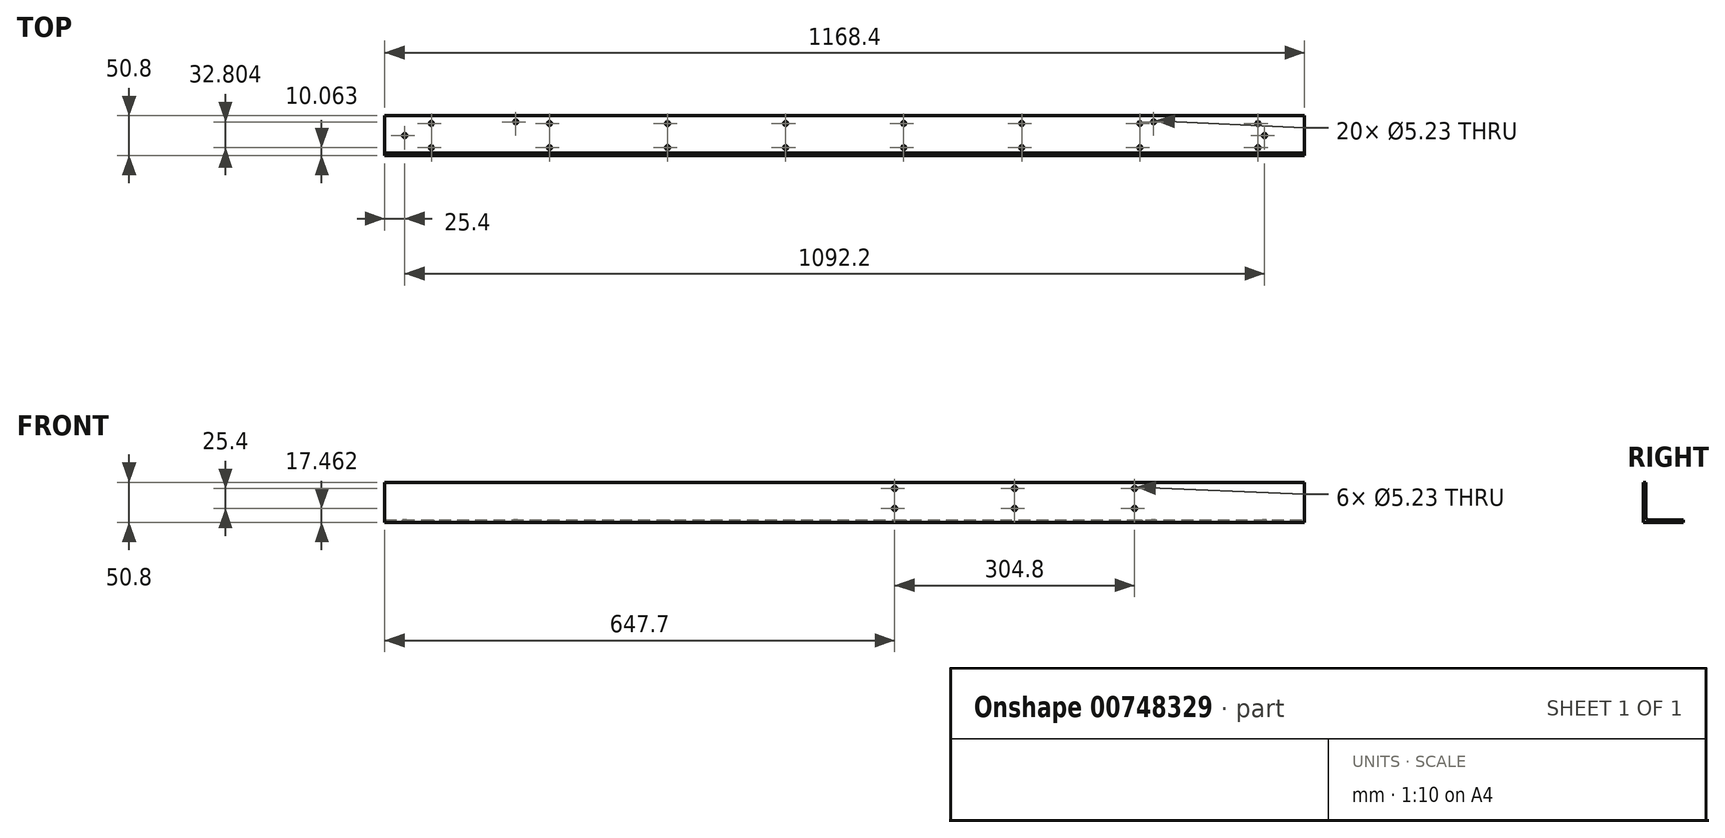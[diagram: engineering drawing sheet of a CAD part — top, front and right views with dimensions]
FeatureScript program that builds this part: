
annotation { "Feature Type Name" : "Feature", "Feature Type Description" : "" }
export const myFeature = defineFeature(function(context is Context, id is Id, definition is map)
    precondition{}
    {
        {
            var Q0;
            Q0=qCreatedBy(makeId("Right.planeOp"),FACE);
            var sketch = newSketch(context, id + "F0", { "sketchPlane" : qUnion([Q0])});
            skLineSegment(sketch, "E0", {"start": v(0, 0) * mm, "end": v(0, -44.45) * mm});
            skLineSegment(sketch, "E1", {"start": v(3.18, -47.62) * mm, "end": v(47.63, -47.62) * mm});
            skLineSegment(sketch, "E2.0", {"start": v(-3.18, -50.8) * mm, "end": v(47.63, -50.8) * mm});
            skLineSegment(sketch, "E2.1", {"start": v(-3.17, 0) * mm, "end": v(-3.18, -50.8) * mm});
            skLineSegment(sketch, "E3", {"start": v(-3.18, 0) * mm, "end": v(0, 0) * mm});
            skLineSegment(sketch, "E4", {"start": v(47.63, -47.62) * mm, "end": v(47.63, -50.8) * mm});
            skPoint(sketch, "E5.visualSharp", {"position": v(0, -47.63) * mm});
            skArc(sketch, "E5.filletArc", {"start": v(0, -44.45) * mm, "mid": v(0.93, -46.7) * mm, "end": v(3.18, -47.63) * mm});
            skSolve(sketch);
        }
        {
            var Q0;
            Q0=makeQuery(id+"F0.imprint","IMPRINT",FACE,{"disambiguationData":[TD([[makeQuery(id+"F0.imprint","IMPRINT",EDGE,{"derivedFrom":sQuery(id+"F0.wireOp",EDGE,"E0")}),-1.0]])]});
            extrude(context, id + "F1", {"entities" : qUnion([Q0]), "oppositeDirection" : true, "depth" : 1168.4 * mm, "offsetDistance" : 25.4 * mm});
        }
        {
            var Q0;
            Q0=makeQuery(id+"F1.opExtrude","SWEPT_FACE",FACE,{"disambiguationData":[OSD([sQuery(id+"F0.wireOp",EDGE,"E2.0")])]});
            var sketch = newSketch(context, id + "F2", { "sketchPlane" : qUnion([Q0])});
            skLineSegment(sketch, "E6", {"start": v(-584.2, -47.62) * mm, "end": v(-584.2, 3.17) * mm, "construction": true});
            skLineSegment(sketch, "E7", {"start": v(-1168.4, -22.22) * mm, "end": v(0, -22.22) * mm, "construction": true});
            skLineSegment(sketch, "E8.0", {"start": v(-1371.6, -37.57) * mm, "end": v(203.2, -37.57) * mm, "construction": true});
            skLineSegment(sketch, "E9.0", {"start": v(-1371.6, -6.88) * mm, "end": v(203.2, -6.88) * mm, "construction": true});
            skLineSegment(sketch, "E10.0", {"start": v(-509.2, -47.62) * mm, "end": v(-509.2, 3.17) * mm, "construction": true});
            skLineSegment(sketch, "E11.0", {"start": v(-359.2, -47.62) * mm, "end": v(-359.2, 3.17) * mm, "construction": true});
            skLineSegment(sketch, "E12.0", {"start": v(-209.2, -47.62) * mm, "end": v(-209.2, 3.17) * mm, "construction": true});
            skLineSegment(sketch, "E13.0", {"start": v(-59.2, -47.62) * mm, "end": v(-59.2, 3.17) * mm, "construction": true});
            skLineSegment(sketch, "E14.0", {"start": v(-659.2, -47.62) * mm, "end": v(-659.2, 3.17) * mm, "construction": true});
            skLineSegment(sketch, "E15.0", {"start": v(-809.2, -47.63) * mm, "end": v(-809.2, 3.17) * mm, "construction": true});
            skLineSegment(sketch, "E16.0", {"start": v(-959.2, -47.63) * mm, "end": v(-959.2, 3.17) * mm, "construction": true});
            skLineSegment(sketch, "E17.0", {"start": v(-1109.2, -47.63) * mm, "end": v(-1109.2, 3.17) * mm, "construction": true});
            skCircle(sketch, "E18", {"center": v(-1109.2, -6.88) * mm, "radius": 2.62 * mm});
            skCircle(sketch, "E19", {"center": v(-1109.2, -37.57) * mm, "radius": 2.62 * mm});
            skCircle(sketch, "E20", {"center": v(-959.2, -6.88) * mm, "radius": 2.62 * mm});
            skCircle(sketch, "E21", {"center": v(-959.2, -37.57) * mm, "radius": 2.62 * mm});
            skCircle(sketch, "E22", {"center": v(-809.2, -6.88) * mm, "radius": 2.62 * mm});
            skCircle(sketch, "E23", {"center": v(-809.2, -37.57) * mm, "radius": 2.62 * mm});
            skCircle(sketch, "E24", {"center": v(-659.2, -6.88) * mm, "radius": 2.62 * mm});
            skCircle(sketch, "E25", {"center": v(-659.2, -37.57) * mm, "radius": 2.62 * mm});
            skCircle(sketch, "E26", {"center": v(-509.2, -6.88) * mm, "radius": 2.62 * mm});
            skCircle(sketch, "E27", {"center": v(-509.2, -37.57) * mm, "radius": 2.62 * mm});
            skCircle(sketch, "E28", {"center": v(-359.2, -6.88) * mm, "radius": 2.62 * mm});
            skCircle(sketch, "E29", {"center": v(-359.2, -37.57) * mm, "radius": 2.62 * mm});
            skCircle(sketch, "E30", {"center": v(-209.2, -6.88) * mm, "radius": 2.62 * mm});
            skCircle(sketch, "E31", {"center": v(-209.2, -37.57) * mm, "radius": 2.62 * mm});
            skCircle(sketch, "E32", {"center": v(-59.2, -6.88) * mm, "radius": 2.62 * mm});
            skCircle(sketch, "E33", {"center": v(-59.2, -37.57) * mm, "radius": 2.62 * mm});
            skSolve(sketch);
        }
        {
            var Q0;
            Q0 = qSketchRegion(id + "F2", true);
            extrude(context, id + "F3", {"entities" : qUnion([Q0]), "operationType" : NewBodyOperationType.REMOVE, "endBound" : BoundingType.THROUGH_ALL, "oppositeDirection" : true, "depth" : 25.4 * mm, "offsetDistance" : 25.4 * mm});
        }
        {
            var Q0;
            Q0=makeQuery(id+"F1.opExtrude","SWEPT_FACE",FACE,{"disambiguationData":[OSD([sQuery(id+"F0.wireOp",EDGE,"E1")])]});
            var sketch = newSketch(context, id + "F4", { "sketchPlane" : qUnion([Q0])});
            skLineSegment(sketch, "E34", {"start": v(-50.8, 47.63) * mm, "end": v(-50.8, 3.18) * mm, "construction": true});
            skCircle(sketch, "E35", {"center": v(-50.8, 22.23) * mm, "radius": 2.62 * mm});
            skLineSegment(sketch, "E36", {"start": v(-1143, 47.63) * mm, "end": v(-1143, 3.18) * mm, "construction": true});
            skCircle(sketch, "E37", {"center": v(-1143, 22.22) * mm, "radius": 2.62 * mm});
            skLineSegment(sketch, "E38", {"start": v(0, 22.23) * mm, "end": v(-1168.4, 22.22) * mm, "construction": true});
            skPoint(sketch, "E38.endSnap0", {"position": v(-1168.4, 25.4) * mm});
            skLineSegment(sketch, "E39", {"start": v(-1168.4, 39.69) * mm, "end": v(0, 39.69) * mm, "construction": true});
            skCircle(sketch, "E40", {"center": v(-1002.07, 39.69) * mm, "radius": 2.62 * mm});
            skCircle(sketch, "E41", {"center": v(-191.74, 39.69) * mm, "radius": 2.62 * mm});
            skSolve(sketch);
        }
        {
            var Q0;
            Q0 = qSketchRegion(id + "F4", true);
            extrude(context, id + "F5", {"entities" : qUnion([Q0]), "operationType" : NewBodyOperationType.REMOVE, "endBound" : BoundingType.THROUGH_ALL, "oppositeDirection" : true, "depth" : 25.4 * mm, "offsetDistance" : 25.4 * mm});
        }
        {
            var Q0;
            Q0=makeQuery(id+"F1.opExtrude","SWEPT_FACE",FACE,{"disambiguationData":[OSD([sQuery(id+"F0.wireOp",EDGE,"E2.1")])]});
            var sketch = newSketch(context, id + "F6", { "sketchPlane" : qUnion([Q0])});
            skLineSegment(sketch, "E42", {"start": v(-1168.4, -7.94) * mm, "end": v(0, -7.94) * mm, "construction": true});
            skLineSegment(sketch, "E43", {"start": v(-368.3, 3.18) * mm, "end": v(-368.3, -47.63) * mm, "construction": true});
            skCircle(sketch, "E44", {"center": v(-368.3, -7.94) * mm, "radius": 2.62 * mm});
            skLineSegment(sketch, "E45.0", {"start": v(-520.7, 3.18) * mm, "end": v(-520.7, -47.63) * mm, "construction": true});
            skLineSegment(sketch, "E46.0", {"start": v(-215.9, 3.18) * mm, "end": v(-215.9, -47.63) * mm, "construction": true});
            skCircle(sketch, "E47", {"center": v(-215.9, -7.94) * mm, "radius": 2.62 * mm});
            skCircle(sketch, "E48", {"center": v(-520.7, -7.94) * mm, "radius": 2.62 * mm});
            skLineSegment(sketch, "E49", {"start": v(0, -33.34) * mm, "end": v(-1168.4, -33.34) * mm, "construction": true});
            skCircle(sketch, "E50", {"center": v(-520.7, -33.34) * mm, "radius": 2.62 * mm});
            skCircle(sketch, "E51", {"center": v(-368.3, -33.34) * mm, "radius": 2.62 * mm});
            skCircle(sketch, "E52", {"center": v(-215.9, -33.34) * mm, "radius": 2.62 * mm});
            skPoint(sketch, "E52.centerSnap0", {"position": v(-215.9, -22.23) * mm});
            skSolve(sketch);
        }
        {
            var Q0;
            Q0 = qSketchRegion(id + "F6", true);
            extrude(context, id + "F7", {"entities" : qUnion([Q0]), "operationType" : NewBodyOperationType.REMOVE, "endBound" : BoundingType.THROUGH_ALL, "oppositeDirection" : true, "depth" : 25.4 * mm, "offsetDistance" : 25.4 * mm});
        }
    });
